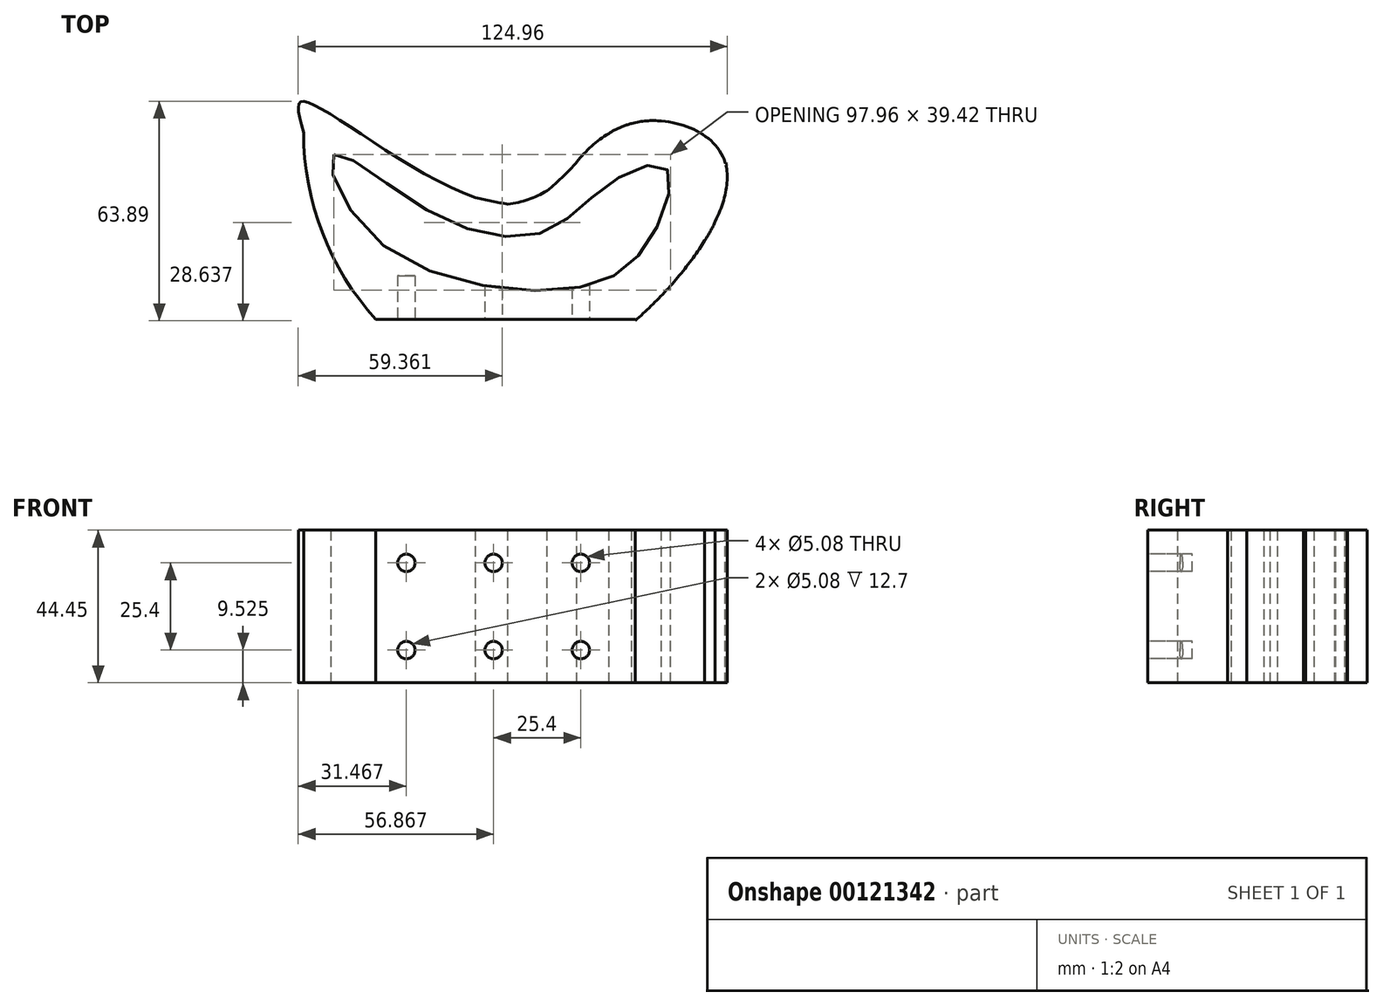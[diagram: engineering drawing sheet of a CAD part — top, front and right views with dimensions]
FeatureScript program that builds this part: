
annotation { "Feature Type Name" : "Feature", "Feature Type Description" : "" }
export const myFeature = defineFeature(function(context is Context, id is Id, definition is map)
    precondition{}
    {
        {
            var Q0;
            Q0=qCreatedBy(makeId("Top.planeOp"),FACE);
            var sketch = newSketch(context, id + "F0", { "sketchPlane" : qUnion([Q0])});
            skLineSegment(sketch, "E0.bottom", {"start": v(63.5, 63.5) * mm, "end": v(-63.5, 63.5) * mm});
            skLineSegment(sketch, "E0.top", {"start": v(63.5, -63.5) * mm, "end": v(-63.5, -63.5) * mm});
            skLineSegment(sketch, "E0.left", {"start": v(63.5, 63.5) * mm, "end": v(63.5, -63.5) * mm});
            skLineSegment(sketch, "E0.right", {"start": v(-63.5, 63.5) * mm, "end": v(-63.5, -63.5) * mm});
            skPoint(sketch, "E0.middle", {"position": v(0, 0) * mm});
            skSolve(sketch);
        }
        {
            var Q0;
            Q0 = qSketchRegion(id + "F0", true);
            extrude(context, id + "F1", {"entities" : qUnion([Q0]), "depth" : 44.45 * mm});
        }
        {
            var Q0;
            Q0=makeQuery(id+"F1.opExtrude","CAP_FACE",FACE,{"disambiguationData":[OSD([sQuery(id+"F0.wireOp",EDGE,"E0.bottom"),sQuery(id+"F0.wireOp",EDGE,"E0.top"),sQuery(id+"F0.wireOp",EDGE,"E0.left"),sQuery(id+"F0.wireOp",EDGE,"E0.right")])],"isStart":false});
            var sketch = newSketch(context, id + "F2", { "sketchPlane" : qUnion([Q0])});
            skFitSpline(sketch, "E1", {"points": [v(-63.5, 63.5) * mm, v(-4.03, 33.55) * mm, v(28.54, 55.87) * mm, v(59.44, 44.95) * mm, v(8.78, -16.23) * mm, v(-39.2, -4.47) * mm, v(-63.5, 54.41) * mm, v(-63.5, 63.5) * mm]});
            skLineSegment(sketch, "E2", {"start": v(-63.5, 54.41) * mm, "end": v(-63.5, 0) * mm});
            skLineSegment(sketch, "E3", {"start": v(-63.5, 0) * mm, "end": v(-42.48, 0) * mm});
            skSolve(sketch);
        }
        {
            var Q0;
            {var subQ2=sQuery(id+"F2.wireOp",EDGE,"E3");Q0=makeQuery(id+"F2.imprint","IMPRINT",FACE,{"disambiguationData":[TD([[makeQuery(id+"F2.imprint","IMPRINT",EDGE,{"derivedFrom":subQ2}),-1.0]])]});}
            var sketch = newSketch(context, id + "F3", { "sketchPlane" : qUnion([Q0])});
            skLineSegment(sketch, "E4.bottom", {"start": v(-42.7, 0) * mm, "end": v(-63.64, 0) * mm});
            skLineSegment(sketch, "E4.top", {"start": v(-42.7, -63.87) * mm, "end": v(-63.64, -63.87) * mm});
            skLineSegment(sketch, "E4.left", {"start": v(-42.7, 0) * mm, "end": v(-42.7, -63.87) * mm});
            skLineSegment(sketch, "E4.right", {"start": v(-63.64, 0) * mm, "end": v(-63.64, -63.87) * mm});
            skLineSegment(sketch, "E5.bottom", {"start": v(-42.7, -63.87) * mm, "end": v(63.26, -63.87) * mm});
            skLineSegment(sketch, "E5.top", {"start": v(-42.7, -20.62) * mm, "end": v(63.26, -20.62) * mm});
            skLineSegment(sketch, "E5.left", {"start": v(-42.7, -63.87) * mm, "end": v(-42.7, -20.62) * mm});
            skLineSegment(sketch, "E5.right", {"start": v(63.26, -63.87) * mm, "end": v(63.26, -20.62) * mm});
            skLineSegment(sketch, "E6.bottom", {"start": v(63.26, -20.62) * mm, "end": v(63.26, -20.62) * mm});
            skLineSegment(sketch, "E6.top", {"start": v(63.26, -24.86) * mm, "end": v(63.26, -24.86) * mm});
            skLineSegment(sketch, "E6.left", {"start": v(63.26, -20.62) * mm, "end": v(63.26, -24.86) * mm});
            skLineSegment(sketch, "E6.right", {"start": v(63.26, -20.62) * mm, "end": v(63.26, -24.86) * mm});
            skLineSegment(sketch, "E7.bottom", {"start": v(63.26, -20.62) * mm, "end": v(47.7, -20.62) * mm});
            skLineSegment(sketch, "E7.top", {"start": v(63.26, 11.18) * mm, "end": v(47.7, 11.18) * mm});
            skLineSegment(sketch, "E7.left", {"start": v(63.26, -20.62) * mm, "end": v(63.26, 11.18) * mm});
            skLineSegment(sketch, "E7.right", {"start": v(47.7, -20.62) * mm, "end": v(47.7, 11.18) * mm});
            skLineSegment(sketch, "E8.bottom", {"start": v(-35.7, 62.7) * mm, "end": v(15.84, 62.7) * mm});
            skLineSegment(sketch, "E8.top", {"start": v(-35.7, 49.46) * mm, "end": v(15.84, 49.46) * mm});
            skLineSegment(sketch, "E8.left", {"start": v(-35.7, 62.7) * mm, "end": v(-35.7, 49.46) * mm});
            skLineSegment(sketch, "E8.right", {"start": v(15.84, 62.7) * mm, "end": v(15.84, 49.46) * mm});
            skLineSegment(sketch, "E9.bottom", {"start": v(-20.4, 49.46) * mm, "end": v(8.75, 49.46) * mm});
            skLineSegment(sketch, "E9.top", {"start": v(-20.4, 42.08) * mm, "end": v(8.75, 42.08) * mm});
            skLineSegment(sketch, "E9.left", {"start": v(-20.4, 49.46) * mm, "end": v(-20.4, 42.08) * mm});
            skLineSegment(sketch, "E9.right", {"start": v(8.75, 49.46) * mm, "end": v(8.75, 42.08) * mm});
            skLineSegment(sketch, "E10.bottom", {"start": v(-13.33, 42.08) * mm, "end": v(3.4, 42.08) * mm});
            skLineSegment(sketch, "E10.top", {"start": v(-13.33, 37) * mm, "end": v(3.4, 37) * mm});
            skLineSegment(sketch, "E10.left", {"start": v(-13.33, 42.08) * mm, "end": v(-13.33, 37) * mm});
            skLineSegment(sketch, "E10.right", {"start": v(3.4, 42.08) * mm, "end": v(3.4, 37) * mm});
            skLineSegment(sketch, "E11.bottom", {"start": v(50.76, 63.4) * mm, "end": v(63.27, 63.4) * mm});
            skLineSegment(sketch, "E11.top", {"start": v(50.76, 55.9) * mm, "end": v(63.27, 55.9) * mm});
            skLineSegment(sketch, "E11.left", {"start": v(50.76, 63.4) * mm, "end": v(50.76, 55.9) * mm});
            skLineSegment(sketch, "E11.right", {"start": v(63.27, 63.4) * mm, "end": v(63.27, 55.9) * mm});
            skLineSegment(sketch, "E12.bottom", {"start": v(-63.1, 29.73) * mm, "end": v(-57.57, 29.73) * mm});
            skLineSegment(sketch, "E12.top", {"start": v(-63.1, 0) * mm, "end": v(-57.57, 0) * mm});
            skLineSegment(sketch, "E12.left", {"start": v(-63.1, 29.73) * mm, "end": v(-63.1, 0) * mm});
            skLineSegment(sketch, "E12.right", {"start": v(-57.57, 29.73) * mm, "end": v(-57.57, 0) * mm});
            skSolve(sketch);
        }
        {
            var Q0;
            Q0 = qSketchRegion(id + "F3", true);
            var Q1;
            Q1=makeQuery(id+"F1.opExtrude","CAP_FACE",FACE,{"disambiguationData":[OSD([sQuery(id+"F0.wireOp",EDGE,"E0.bottom"),sQuery(id+"F0.wireOp",EDGE,"E0.top"),sQuery(id+"F0.wireOp",EDGE,"E0.left"),sQuery(id+"F0.wireOp",EDGE,"E0.right")])],"isStart":true});
            extrude(context, id + "F4", {"entities" : qUnion([Q0]), "operationType" : NewBodyOperationType.REMOVE, "endBound" : BoundingType.UP_TO_SURFACE, "oppositeDirection" : true, "endBoundEntityFace" : qUnion([Q1]), "depth" : 25.4 * mm});
        }
        {
            var Q0;
            {var subQ0=sQuery(id+"F2.wireOp",EDGE,"E2");Q0=makeQuery(id+"F2.imprint","IMPRINT",FACE,{"disambiguationData":[TD([[makeQuery(id+"F2.imprint","IMPRINT",EDGE,{"derivedFrom":subQ0}),1.0]])]});}
            var sketch = newSketch(context, id + "F5", { "sketchPlane" : qUnion([Q0])});
            skArc(sketch, "E13", {"start": v(-63.4, 55.46) * mm, "mid": v(-55.8, 26.58) * mm, "end": v(-42.17, 0) * mm});
            skLineSegment(sketch, "E14", {"start": v(-63.4, 55.46) * mm, "end": v(-63.4, 0) * mm});
            skLineSegment(sketch, "E15", {"start": v(-63.4, 0) * mm, "end": v(-42.17, 0) * mm});
            skSolve(sketch);
        }
        {
            var Q0;
            Q0 = qSketchRegion(id + "F5", true);
            var Q1;
            Q1=makeQuery(id+"F1.opExtrude","CAP_FACE",FACE,{"disambiguationData":[OSD([sQuery(id+"F0.wireOp",EDGE,"E0.bottom"),sQuery(id+"F0.wireOp",EDGE,"E0.top"),sQuery(id+"F0.wireOp",EDGE,"E0.left"),sQuery(id+"F0.wireOp",EDGE,"E0.right")])],"isStart":true});
            extrude(context, id + "F6", {"entities" : qUnion([Q0]), "operationType" : NewBodyOperationType.REMOVE, "endBound" : BoundingType.UP_TO_SURFACE, "oppositeDirection" : true, "endBoundEntityFace" : qUnion([Q1]), "depth" : 25.4 * mm});
        }
        {
            var Q0;
            {var subQ0=sQuery(id+"F2.wireOp",EDGE,"E1");var subQ3=makeQuery(id+"F2.imprint","INTERSECT",VERTEX,{"derivedFrom":[subQ0,sQuery(id+"F2.wireOp",EDGE,"E3")]});Q0=makeQuery(id+"F2.imprint","IMPRINT",FACE,{"disambiguationData":[TD([[makeQuery(id+"F2.imprint","IMPRINT",EDGE,{"disambiguationData":[TD([[subQ3,1.0]])],"derivedFrom":subQ0}),-1.0]])]});}
            var sketch = newSketch(context, id + "F7", { "sketchPlane" : qUnion([Q0])});
            skArc(sketch, "E16", {"start": v(-42.2, 0) * mm, "mid": v(-19.93, -18.2) * mm, "end": v(8.77, -16.2) * mm});
            skLineSegment(sketch, "E17", {"start": v(-42.2, 0) * mm, "end": v(-42.2, -20.45) * mm});
            skLineSegment(sketch, "E18", {"start": v(-42.2, -20.45) * mm, "end": v(9.07, -20.45) * mm});
            skLineSegment(sketch, "E19", {"start": v(9.07, -20.45) * mm, "end": v(8.77, -16.2) * mm});
            skSolve(sketch);
        }
        {
            var Q0;
            {var subQ0=sQuery(id+"F7.wireOp",EDGE,"E18");Q0=makeQuery(id+"F7.imprint","IMPRINT",FACE,{"disambiguationData":[TD([[makeQuery(id+"F7.imprint","IMPRINT",EDGE,{"derivedFrom":subQ0}),1.0]])]});}
            extrude(context, id + "F8", {"entities" : qUnion([Q0]), "operationType" : NewBodyOperationType.REMOVE, "oppositeDirection" : true, "depth" : 44.45 * mm});
        }
        {
            var Q0;
            {var subQ2=sQuery(id+"F2.wireOp",EDGE,"E3");Q0=makeQuery(id+"F2.imprint","IMPRINT",FACE,{"disambiguationData":[TD([[makeQuery(id+"F2.imprint","IMPRINT",EDGE,{"derivedFrom":subQ2}),-1.0]])]});}
            var sketch = newSketch(context, id + "F9", { "sketchPlane" : qUnion([Q0])});
            skArc(sketch, "E20", {"start": v(8.78, -16.23) * mm, "mid": v(33.69, 0.22) * mm, "end": v(53.2, 22.81) * mm});
            skArc(sketch, "E21", {"start": v(53.2, 22.81) * mm, "mid": v(58.1, 33.4) * mm, "end": v(59.41, 44.99) * mm});
            skLineSegment(sketch, "E22", {"start": v(8.78, -16.23) * mm, "end": v(8.78, -20.73) * mm});
            skLineSegment(sketch, "E23", {"start": v(8.78, -20.73) * mm, "end": v(67.33, -23.11) * mm});
            skLineSegment(sketch, "E24", {"start": v(67.33, -23.11) * mm, "end": v(67.33, 48.2) * mm});
            skLineSegment(sketch, "E25", {"start": v(67.33, 48.2) * mm, "end": v(59.41, 44.99) * mm});
            skSolve(sketch);
        }
        {
            var Q0;
            Q0 = qSketchRegion(id + "F9", true);
            var Q1;
            Q1=makeQuery(id+"F1.opExtrude","CAP_FACE",FACE,{"disambiguationData":[OSD([sQuery(id+"F0.wireOp",EDGE,"E0.bottom"),sQuery(id+"F0.wireOp",EDGE,"E0.top"),sQuery(id+"F0.wireOp",EDGE,"E0.left"),sQuery(id+"F0.wireOp",EDGE,"E0.right")])],"isStart":true});
            extrude(context, id + "F10", {"entities" : qUnion([Q0]), "operationType" : NewBodyOperationType.ADD, "endBound" : BoundingType.UP_TO_SURFACE, "oppositeDirection" : true, "endBoundEntityFace" : qUnion([Q1]), "depth" : 25.4 * mm});
        }
        {
            var Q0;
            Q0 = qSketchRegion(id + "F9", true);
            extrude(context, id + "F11", {"entities" : qUnion([Q0]), "operationType" : NewBodyOperationType.REMOVE, "oppositeDirection" : true, "depth" : 44.45 * mm});
        }
        {
            var Q0;
            {var subQ0=sQuery(id+"F2.wireOp",EDGE,"E1");var subQ3=makeQuery(id+"F2.imprint","INTERSECT",VERTEX,{"derivedFrom":[subQ0,sQuery(id+"F2.wireOp",EDGE,"E3")]});Q0=makeQuery(id+"F2.imprint","IMPRINT",FACE,{"disambiguationData":[TD([[makeQuery(id+"F2.imprint","IMPRINT",EDGE,{"disambiguationData":[TD([[subQ3,1.0]])],"derivedFrom":subQ0}),-1.0]])]});}
            var sketch = newSketch(context, id + "F12", { "sketchPlane" : qUnion([Q0])});
            skArc(sketch, "E26", {"start": v(59.44, 45.3) * mm, "mid": v(46.04, 56.58) * mm, "end": v(28.55, 55.84) * mm});
            skArc(sketch, "E27", {"start": v(28.55, 55.84) * mm, "mid": v(20.96, 50.99) * mm, "end": v(14.97, 44.26) * mm});
            skArc(sketch, "E28", {"start": v(-3.97, 33.58) * mm, "mid": v(6.56, 37.03) * mm, "end": v(14.97, 44.26) * mm});
            skArc(sketch, "E29", {"start": v(-63.11, 63) * mm, "mid": v(-35.87, 43.6) * mm, "end": v(-3.97, 33.58) * mm});
            skLineSegment(sketch, "E30", {"start": v(-63.11, 63) * mm, "end": v(-66.26, 66.09) * mm});
            skLineSegment(sketch, "E31", {"start": v(-66.26, 66.09) * mm, "end": v(79.94, 67.8) * mm});
            skLineSegment(sketch, "E32", {"start": v(79.94, 67.8) * mm, "end": v(65.07, 43.9) * mm});
            skLineSegment(sketch, "E33", {"start": v(65.07, 43.9) * mm, "end": v(59.44, 45.3) * mm});
            skSolve(sketch);
        }
        {
            var Q0;
            Q0 = qSketchRegion(id + "F12", true);
            extrude(context, id + "F13", {"entities" : qUnion([Q0]), "operationType" : NewBodyOperationType.REMOVE, "oppositeDirection" : true, "depth" : 44.45 * mm});
        }
        {
            var Q0;
            Q0=makeQuery(id+"F4.boolean.opBoolean","COPY",FACE,{"derivedFrom":makeQuery(id+"F4.opExtrude","SWEPT_FACE",FACE,{"disambiguationData":[OSD([sQuery(id+"F3.wireOp",EDGE,"E5.right"),sQuery(id+"F3.wireOp",EDGE,"E6.right"),sQuery(id+"F3.wireOp",EDGE,"E7.left")])]})});
            var sketch = newSketch(context, id + "F14", { "sketchPlane" : qUnion([Q0])});
            skLineSegment(sketch, "E34.bottom", {"start": v(22.95, 44.45) * mm, "end": v(63.5, 44.45) * mm});
            skLineSegment(sketch, "E34.top", {"start": v(22.95, 0) * mm, "end": v(63.5, 0) * mm});
            skLineSegment(sketch, "E34.left", {"start": v(22.95, 44.45) * mm, "end": v(22.95, 0) * mm});
            skLineSegment(sketch, "E34.right", {"start": v(63.5, 44.45) * mm, "end": v(63.5, 0) * mm});
            skSolve(sketch);
        }
        {
            var Q0;
            Q0 = qSketchRegion(id + "F14", true);
            extrude(context, id + "F15", {"entities" : qUnion([Q0]), "operationType" : NewBodyOperationType.REMOVE, "oppositeDirection" : true, "depth" : 25.4 * mm});
        }
        {
            var Q0;
            Q0=makeQuery(id+"F4.boolean.opBoolean","COPY",FACE,{"derivedFrom":makeQuery(id+"F4.opExtrude","SWEPT_FACE",FACE,{"disambiguationData":[OSD([sQuery(id+"F3.wireOp",EDGE,"E5.top")])]})});
            var sketch = newSketch(context, id + "F16", { "sketchPlane" : qUnion([Q0])});
            skLineSegment(sketch, "E35.bottom", {"start": v(-42.7, 44.45) * mm, "end": v(8.78, 44.45) * mm});
            skLineSegment(sketch, "E35.top", {"start": v(-42.7, 0) * mm, "end": v(8.78, 0) * mm});
            skLineSegment(sketch, "E35.left", {"start": v(-42.7, 44.45) * mm, "end": v(-42.7, 0) * mm});
            skLineSegment(sketch, "E35.right", {"start": v(8.78, 44.45) * mm, "end": v(8.78, 0) * mm});
            skSolve(sketch);
        }
        {
            var Q0;
            Q0 = qSketchRegion(id + "F16", true);
            var Q1;
            Q1=makeQuery(id+"F8.boolean.opBoolean","COPY",FACE,{"derivedFrom":makeQuery(id+"F8.opExtrude","SWEPT_FACE",FACE,{"disambiguationData":[OSD([sQuery(id+"F7.wireOp",EDGE,"E18")])]})});
            extrude(context, id + "F17", {"entities" : qUnion([Q0]), "operationType" : NewBodyOperationType.REMOVE, "endBound" : BoundingType.UP_TO_SURFACE, "oppositeDirection" : true, "endBoundEntityFace" : qUnion([Q1]), "depth" : 25.4 * mm});
        }
        {
            var Q0;
            Q0=makeQuery(id+"F4.boolean.opBoolean","COPY",FACE,{"derivedFrom":makeQuery(id+"F4.opExtrude","SWEPT_FACE",FACE,{"disambiguationData":[OSD([sQuery(id+"F3.wireOp",EDGE,"E4.left")])]})});
            var sketch = newSketch(context, id + "F18", { "sketchPlane" : qUnion([Q0])});
            skLineSegment(sketch, "E36.bottom", {"start": v(20.45, 0) * mm, "end": v(0, 0) * mm});
            skLineSegment(sketch, "E36.top", {"start": v(20.45, 44.45) * mm, "end": v(0, 44.45) * mm});
            skLineSegment(sketch, "E36.left", {"start": v(20.45, 0) * mm, "end": v(20.45, 44.45) * mm});
            skLineSegment(sketch, "E36.right", {"start": v(0, 0) * mm, "end": v(0, 44.45) * mm});
            skSolve(sketch);
        }
        {
            var Q0;
            Q0 = qSketchRegion(id + "F18", true);
            var Q1;
            Q1=makeQuery(id+"F8.boolean.opBoolean","COPY",FACE,{"derivedFrom":makeQuery(id+"F8.opExtrude","SWEPT_FACE",FACE,{"disambiguationData":[OSD([sQuery(id+"F7.wireOp",EDGE,"E17")])]})});
            extrude(context, id + "F19", {"entities" : qUnion([Q0]), "operationType" : NewBodyOperationType.REMOVE, "endBound" : BoundingType.UP_TO_SURFACE, "oppositeDirection" : true, "endBoundEntityFace" : qUnion([Q1]), "depth" : 25.4 * mm});
        }
        {
            var Q0;
            Q0=makeQuery(id+"F1.opExtrude","SWEPT_FACE",FACE,{"disambiguationData":[OSD([sQuery(id+"F0.wireOp",EDGE,"E0.right")])]});
            var sketch = newSketch(context, id + "F20", { "sketchPlane" : qUnion([Q0])});
            skLineSegment(sketch, "E37.bottom", {"start": v(0, 44.45) * mm, "end": v(-63.38, 44.45) * mm});
            skLineSegment(sketch, "E37.top", {"start": v(0, 0) * mm, "end": v(-63.38, 0) * mm});
            skLineSegment(sketch, "E37.left", {"start": v(0, 44.45) * mm, "end": v(0, 0) * mm});
            skLineSegment(sketch, "E37.right", {"start": v(-63.38, 44.45) * mm, "end": v(-63.38, 0) * mm});
            skSolve(sketch);
        }
        {
            var Q0;
            Q0 = qSketchRegion(id + "F20", true);
            var Q1;
            Q1=makeQuery(id+"F6.boolean.opBoolean","COPY",FACE,{"derivedFrom":makeQuery(id+"F6.opExtrude","SWEPT_FACE",FACE,{"disambiguationData":[OSD([sQuery(id+"F5.wireOp",EDGE,"E14")])]})});
            extrude(context, id + "F21", {"entities" : qUnion([Q0]), "operationType" : NewBodyOperationType.REMOVE, "endBound" : BoundingType.UP_TO_SURFACE, "oppositeDirection" : true, "endBoundEntityFace" : qUnion([Q1]), "depth" : 25.4 * mm});
        }
        {
            var Q0;
            Q0 = qSketchRegion(id + "F2", true);
            extrude(context, id + "F22", {"entities" : qUnion([Q0]), "operationType" : NewBodyOperationType.ADD, "oppositeDirection" : true, "depth" : 44.45 * mm});
        }
        {
            var Q0;
            {var subQ0=sQuery(id+"F2.wireOp",EDGE,"E3");var subQ1=sQuery(id+"F2.wireOp",EDGE,"E2");var subQ2=sQuery(id+"F2.wireOp",EDGE,"E1");var subQ5=sQuery(id+"F0.wireOp",EDGE,"E0.right");var subQ7=sQuery(id+"F0.wireOp",EDGE,"E0.bottom");var subQ22=sQuery(id+"F0.wireOp",EDGE,"E0.top");var subQ24=sQuery(id+"F9.wireOp",EDGE,"E22");var subQ25=sQuery(id+"F0.wireOp",EDGE,"E0.left");var subQ26=sQuery(id+"F9.wireOp",EDGE,"E20");var subQ27=sQuery(id+"F9.wireOp",EDGE,"E25");var subQ31=sQuery(id+"F9.wireOp",EDGE,"E21");Q0=makeQuery(id+"F22.boolean.opBoolean","MERGE",FACE,{"derivedFrom":[makeQuery(id+"F11.boolean.opBoolean","SPLIT",FACE,{"disambiguationData":[TD([makeQuery(id+"F1.opExtrude","SWEPT_FACE",FACE,{"disambiguationData":[OSD([subQ7])]})])],"derivedFrom":makeQuery(id+"F10.boolean.opBoolean","MERGE",FACE,{"derivedFrom":[makeQuery(id+"F1.opExtrude","CAP_FACE",FACE,{"disambiguationData":[OSD([subQ7,subQ22,subQ25,subQ5])],"isStart":false}),makeQuery(id+"F10.opExtrude","CAP_FACE",FACE,{"disambiguationData":[OSD([subQ26,subQ31,subQ24,sQuery(id+"F9.wireOp",EDGE,"E23"),sQuery(id+"F9.wireOp",EDGE,"E24"),subQ27])],"isStart":true})]})}),makeQuery(id+"F22.opExtrude","CAP_FACE",FACE,{"disambiguationData":[OSD([subQ2,subQ1,subQ0])],"isStart":true})]});}
            var sketch = newSketch(context, id + "F23", { "sketchPlane" : qUnion([Q0])});
            skArc(sketch, "E38", {"start": v(-63.5, 54.41) * mm, "mid": v(-58.06, 25.25) * mm, "end": v(-42.48, 0) * mm});
            skLineSegment(sketch, "E39", {"start": v(-63.5, 54.41) * mm, "end": v(-63.5, 0) * mm});
            skLineSegment(sketch, "E40", {"start": v(-63.5, 0) * mm, "end": v(-42.48, 0) * mm});
            skSolve(sketch);
        }
        {
            var Q0;
            Q0 = qSketchRegion(id + "F23", true);
            extrude(context, id + "F24", {"entities" : qUnion([Q0]), "operationType" : NewBodyOperationType.REMOVE, "oppositeDirection" : true, "depth" : 44.45 * mm});
        }
        {
            var Q0;
            {var subQ0=sQuery(id+"F2.wireOp",EDGE,"E3");var subQ1=sQuery(id+"F2.wireOp",EDGE,"E2");var subQ2=sQuery(id+"F2.wireOp",EDGE,"E1");var subQ5=sQuery(id+"F0.wireOp",EDGE,"E0.right");var subQ7=sQuery(id+"F0.wireOp",EDGE,"E0.bottom");var subQ22=sQuery(id+"F0.wireOp",EDGE,"E0.top");var subQ24=sQuery(id+"F9.wireOp",EDGE,"E22");var subQ25=sQuery(id+"F0.wireOp",EDGE,"E0.left");var subQ26=sQuery(id+"F9.wireOp",EDGE,"E20");var subQ27=sQuery(id+"F9.wireOp",EDGE,"E25");var subQ31=sQuery(id+"F9.wireOp",EDGE,"E21");Q0=makeQuery(id+"F22.boolean.opBoolean","MERGE",FACE,{"derivedFrom":[makeQuery(id+"F11.boolean.opBoolean","SPLIT",FACE,{"disambiguationData":[TD([makeQuery(id+"F1.opExtrude","SWEPT_FACE",FACE,{"disambiguationData":[OSD([subQ7])]})])],"derivedFrom":makeQuery(id+"F10.boolean.opBoolean","MERGE",FACE,{"derivedFrom":[makeQuery(id+"F1.opExtrude","CAP_FACE",FACE,{"disambiguationData":[OSD([subQ7,subQ22,subQ25,subQ5])],"isStart":false}),makeQuery(id+"F10.opExtrude","CAP_FACE",FACE,{"disambiguationData":[OSD([subQ26,subQ31,subQ24,sQuery(id+"F9.wireOp",EDGE,"E23"),sQuery(id+"F9.wireOp",EDGE,"E24"),subQ27])],"isStart":true})]})}),makeQuery(id+"F22.opExtrude","CAP_FACE",FACE,{"disambiguationData":[OSD([subQ2,subQ1,subQ0])],"isStart":true})]});}
            var sketch = newSketch(context, id + "F25", { "sketchPlane" : qUnion([Q0])});
            skLineSegment(sketch, "E41.bottom", {"start": v(-42.48, 0) * mm, "end": v(33, 0) * mm});
            skLineSegment(sketch, "E41.top", {"start": v(-42.48, -21.75) * mm, "end": v(33, -21.75) * mm});
            skLineSegment(sketch, "E41.left", {"start": v(-42.48, 0) * mm, "end": v(-42.48, -21.75) * mm});
            skLineSegment(sketch, "E41.right", {"start": v(33, 0) * mm, "end": v(33, -21.75) * mm});
            skSolve(sketch);
        }
        {
            var Q0;
            Q0 = qSketchRegion(id + "F25", true);
            extrude(context, id + "F26", {"entities" : qUnion([Q0]), "operationType" : NewBodyOperationType.REMOVE, "oppositeDirection" : true, "depth" : 44.45 * mm});
        }
        {
            var Q0;
            Q0=makeQuery(id+"F26.boolean.opBoolean","COPY",FACE,{"derivedFrom":makeQuery(id+"F26.opExtrude","SWEPT_FACE",FACE,{"disambiguationData":[OSD([sQuery(id+"F25.wireOp",EDGE,"E41.bottom")])]})});
            var sketch = newSketch(context, id + "F27", { "sketchPlane" : qUnion([Q0])});
            skCircle(sketch, "E42", {"center": v(-33.6, 34.92) * mm, "radius": 2.54 * mm});
            skCircle(sketch, "E43.0.1.0", {"center": v(-33.6, 9.52) * mm, "radius": 2.54 * mm});
            skCircle(sketch, "E43.1.0.0", {"center": v(-8.2, 34.92) * mm, "radius": 2.54 * mm});
            skCircle(sketch, "E43.1.1.0", {"center": v(-8.2, 9.52) * mm, "radius": 2.54 * mm});
            skCircle(sketch, "E43.2.0.0", {"center": v(17.2, 34.92) * mm, "radius": 2.54 * mm});
            skCircle(sketch, "E43.2.1.0", {"center": v(17.2, 9.52) * mm, "radius": 2.54 * mm});
            skLineSegment(sketch, "E43.direction1", {"start": v(-33.6, 34.92) * mm, "end": v(-8.2, 34.92) * mm, "construction": true});
            skLineSegment(sketch, "E43.direction2", {"start": v(-33.6, 34.92) * mm, "end": v(-33.6, 9.52) * mm, "construction": true});
            skSolve(sketch);
        }
        {
            var Q0;
            Q0 = qSketchRegion(id + "F27", true);
            extrude(context, id + "F28", {"entities" : qUnion([Q0]), "operationType" : NewBodyOperationType.REMOVE, "oppositeDirection" : true, "depth" : 12.7 * mm});
        }
        {
            var Q0;
            {var subQ0=sQuery(id+"F2.wireOp",EDGE,"E3");var subQ1=sQuery(id+"F2.wireOp",EDGE,"E2");var subQ2=sQuery(id+"F2.wireOp",EDGE,"E1");var subQ5=sQuery(id+"F0.wireOp",EDGE,"E0.right");var subQ7=sQuery(id+"F0.wireOp",EDGE,"E0.bottom");var subQ22=sQuery(id+"F0.wireOp",EDGE,"E0.top");var subQ24=sQuery(id+"F9.wireOp",EDGE,"E22");var subQ25=sQuery(id+"F0.wireOp",EDGE,"E0.left");var subQ26=sQuery(id+"F9.wireOp",EDGE,"E20");var subQ27=sQuery(id+"F9.wireOp",EDGE,"E25");var subQ31=sQuery(id+"F9.wireOp",EDGE,"E21");Q0=makeQuery(id+"F22.boolean.opBoolean","MERGE",FACE,{"derivedFrom":[makeQuery(id+"F11.boolean.opBoolean","SPLIT",FACE,{"disambiguationData":[TD([makeQuery(id+"F1.opExtrude","SWEPT_FACE",FACE,{"disambiguationData":[OSD([subQ7])]})])],"derivedFrom":makeQuery(id+"F10.boolean.opBoolean","MERGE",FACE,{"derivedFrom":[makeQuery(id+"F1.opExtrude","CAP_FACE",FACE,{"disambiguationData":[OSD([subQ7,subQ22,subQ25,subQ5])],"isStart":false}),makeQuery(id+"F10.opExtrude","CAP_FACE",FACE,{"disambiguationData":[OSD([subQ26,subQ31,subQ24,sQuery(id+"F9.wireOp",EDGE,"E23"),sQuery(id+"F9.wireOp",EDGE,"E24"),subQ27])],"isStart":true})]})}),makeQuery(id+"F22.opExtrude","CAP_FACE",FACE,{"disambiguationData":[OSD([subQ2,subQ1,subQ0])],"isStart":true})]});}
            var sketch = newSketch(context, id + "F29", { "sketchPlane" : qUnion([Q0])});
            skFitSpline(sketch, "E44", {"points": [v(-54.68, 47.97) * mm, v(-28.2, 32.2) * mm, v(6.3, 25.38) * mm, v(26.33, 40.14) * mm, v(42.2, 43.9) * mm, v(37.5, 23.47) * mm, v(16.25, 9.28) * mm, v(-42.74, 23.59) * mm, v(-54.68, 47.97) * mm]});
            skSolve(sketch);
        }
        {
            var Q0;
            Q0 = qSketchRegion(id + "F29", true);
            var Q1;
            {var subQ0=sQuery(id+"F2.wireOp",EDGE,"E3");var subQ1=sQuery(id+"F2.wireOp",EDGE,"E2");var subQ2=sQuery(id+"F2.wireOp",EDGE,"E1");var subQ5=sQuery(id+"F0.wireOp",EDGE,"E0.right");var subQ7=sQuery(id+"F0.wireOp",EDGE,"E0.bottom");var subQ22=sQuery(id+"F0.wireOp",EDGE,"E0.top");var subQ24=sQuery(id+"F9.wireOp",EDGE,"E22");var subQ25=sQuery(id+"F0.wireOp",EDGE,"E0.left");var subQ26=sQuery(id+"F9.wireOp",EDGE,"E20");var subQ27=sQuery(id+"F9.wireOp",EDGE,"E25");var subQ31=sQuery(id+"F9.wireOp",EDGE,"E21");Q1=makeQuery(id+"F22.boolean.opBoolean","MERGE",FACE,{"derivedFrom":[makeQuery(id+"F11.boolean.opBoolean","SPLIT",FACE,{"disambiguationData":[TD([makeQuery(id+"F1.opExtrude","SWEPT_FACE",FACE,{"disambiguationData":[OSD([subQ7])]})])],"derivedFrom":makeQuery(id+"F10.boolean.opBoolean","MERGE",FACE,{"derivedFrom":[makeQuery(id+"F1.opExtrude","CAP_FACE",FACE,{"disambiguationData":[OSD([subQ7,subQ22,subQ25,subQ5])],"isStart":true}),makeQuery(id+"F10.opExtrude","CAP_FACE",FACE,{"disambiguationData":[OSD([subQ26,subQ31,subQ24,sQuery(id+"F9.wireOp",EDGE,"E23"),sQuery(id+"F9.wireOp",EDGE,"E24"),subQ27])],"isStart":false})]})}),makeQuery(id+"F22.opExtrude","CAP_FACE",FACE,{"disambiguationData":[OSD([subQ2,subQ1,subQ0])],"isStart":false})]});}
            extrude(context, id + "F30", {"entities" : qUnion([Q0]), "operationType" : NewBodyOperationType.REMOVE, "endBound" : BoundingType.UP_TO_SURFACE, "oppositeDirection" : true, "endBoundEntityFace" : qUnion([Q1]), "depth" : 25.4 * mm});
        }
    });
